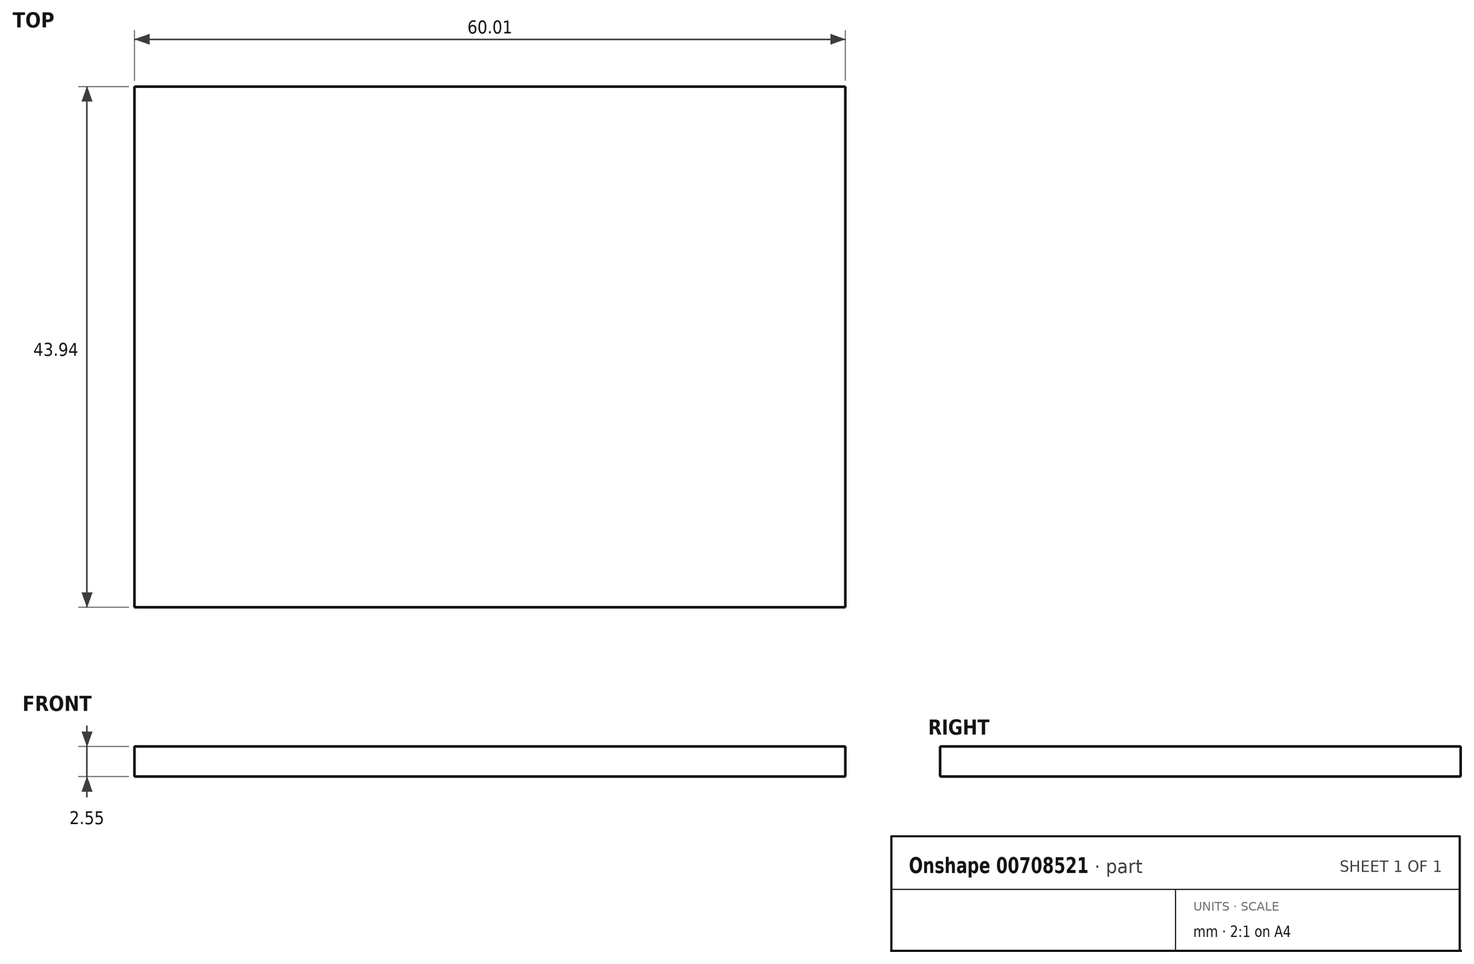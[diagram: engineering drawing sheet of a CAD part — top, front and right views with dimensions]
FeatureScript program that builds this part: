
annotation { "Feature Type Name" : "Feature", "Feature Type Description" : "" }
export const myFeature = defineFeature(function(context is Context, id is Id, definition is map)
    precondition{}
    {
        {
            var Q0;
            Q0=qCreatedBy(makeId("Front.planeOp"),FACE);
            var sketch = newSketch(context, id + "F0", { "sketchPlane" : qUnion([Q0])});
            skLineSegment(sketch, "E0.bottom", {"start": v(0, 0) * mm, "end": v(-60, 0) * mm});
            skLineSegment(sketch, "E0.top", {"start": v(0, -2.55) * mm, "end": v(-60, -2.55) * mm});
            skLineSegment(sketch, "E0.left", {"start": v(0, 0) * mm, "end": v(0, -2.55) * mm});
            skLineSegment(sketch, "E0.right", {"start": v(-60, 0) * mm, "end": v(-60, -2.55) * mm});
            skSolve(sketch);
        }
        {
            var Q0;
            Q0=makeQuery(id+"F0.imprint","IMPRINT",FACE,{"disambiguationData":[TD([[makeQuery(id+"F0.imprint","IMPRINT",EDGE,{"derivedFrom":sQuery(id+"F0.wireOp",EDGE,"E0.bottom")}),1.0]])]});
            extrude(context, id + "F1", {"entities" : qUnion([Q0]), "depth" : 43.94 * mm, "offsetDistance" : 25.4 * mm});
        }
    });
